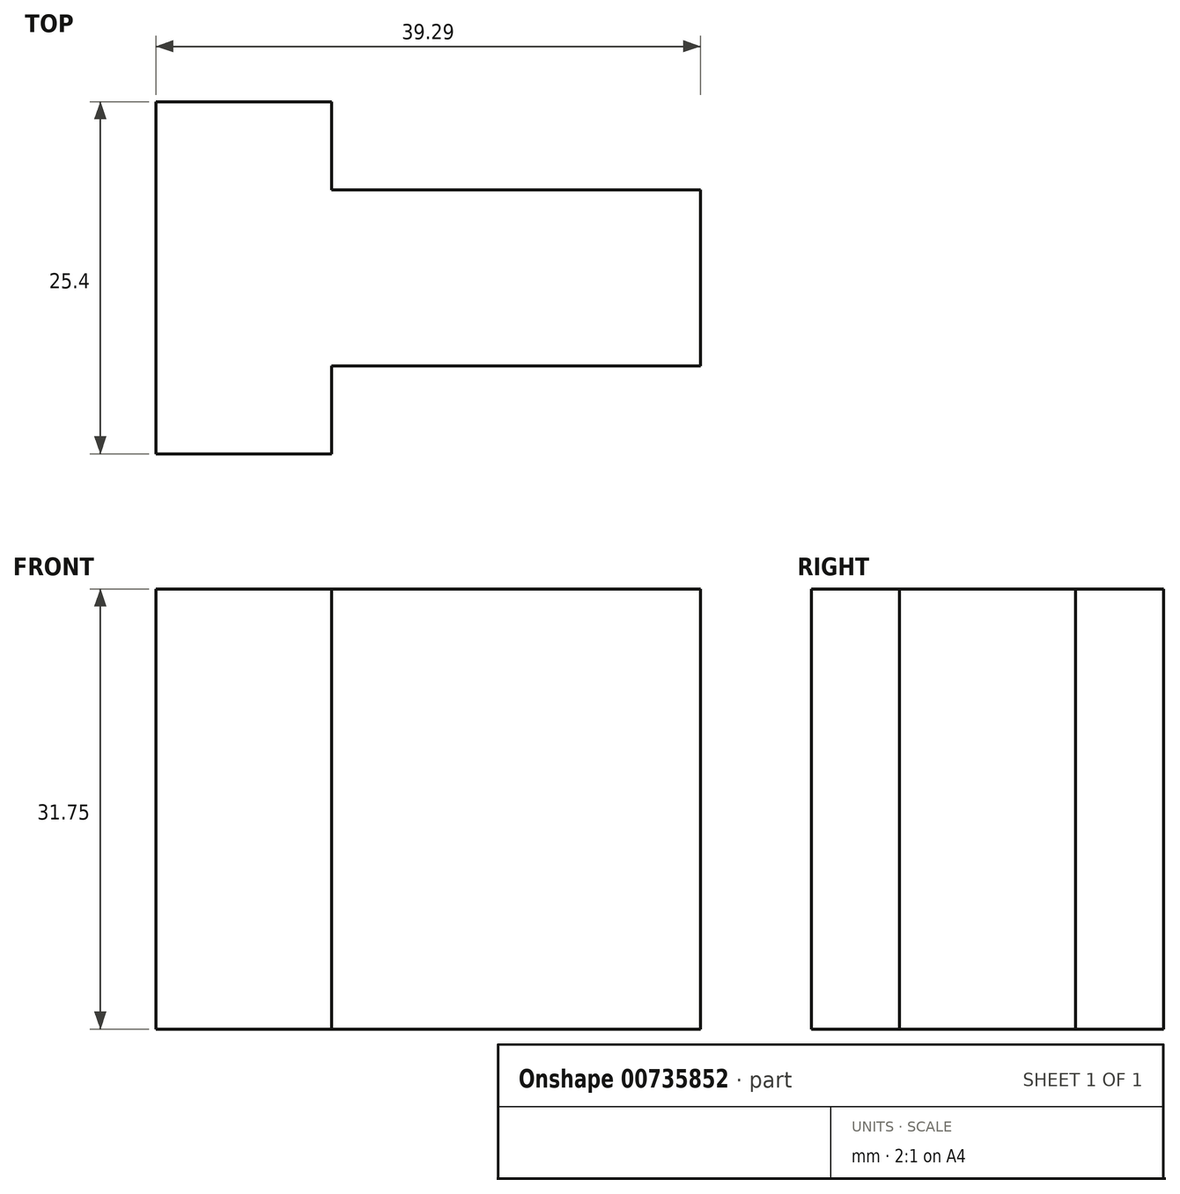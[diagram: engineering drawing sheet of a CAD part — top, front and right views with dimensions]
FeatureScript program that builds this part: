
annotation { "Feature Type Name" : "Feature", "Feature Type Description" : "" }
export const myFeature = defineFeature(function(context is Context, id is Id, definition is map)
    precondition{}
    {
        {
            var Q0;
            Q0=qCreatedBy(makeId("Top.planeOp"),FACE);
            var sketch = newSketch(context, id + "F0", { "sketchPlane" : qUnion([Q0])});
            skLineSegment(sketch, "E0", {"start": v(0, 0) * mm, "end": v(12.7, 0) * mm});
            skLineSegment(sketch, "E1", {"start": v(12.7, 0) * mm, "end": v(12.7, 6.35) * mm});
            skLineSegment(sketch, "E2", {"start": v(12.7, 6.35) * mm, "end": v(39.29, 6.35) * mm});
            skLineSegment(sketch, "E3", {"start": v(39.29, 6.35) * mm, "end": v(39.29, 19.05) * mm});
            skLineSegment(sketch, "E4", {"start": v(39.29, 19.05) * mm, "end": v(12.7, 19.05) * mm});
            skLineSegment(sketch, "E5", {"start": v(12.7, 19.05) * mm, "end": v(12.7, 25.4) * mm});
            skLineSegment(sketch, "E6", {"start": v(12.7, 25.4) * mm, "end": v(0, 25.4) * mm});
            skLineSegment(sketch, "E7", {"start": v(0, 25.4) * mm, "end": v(0, 0) * mm});
            skSolve(sketch);
        }
        {
            var Q0;
            Q0 = qSketchRegion(id + "F0", true);
            extrude(context, id + "F1", {"entities" : qUnion([Q0]), "depth" : 31.75 * mm, "offsetDistance" : 25.4 * mm});
        }
    });
